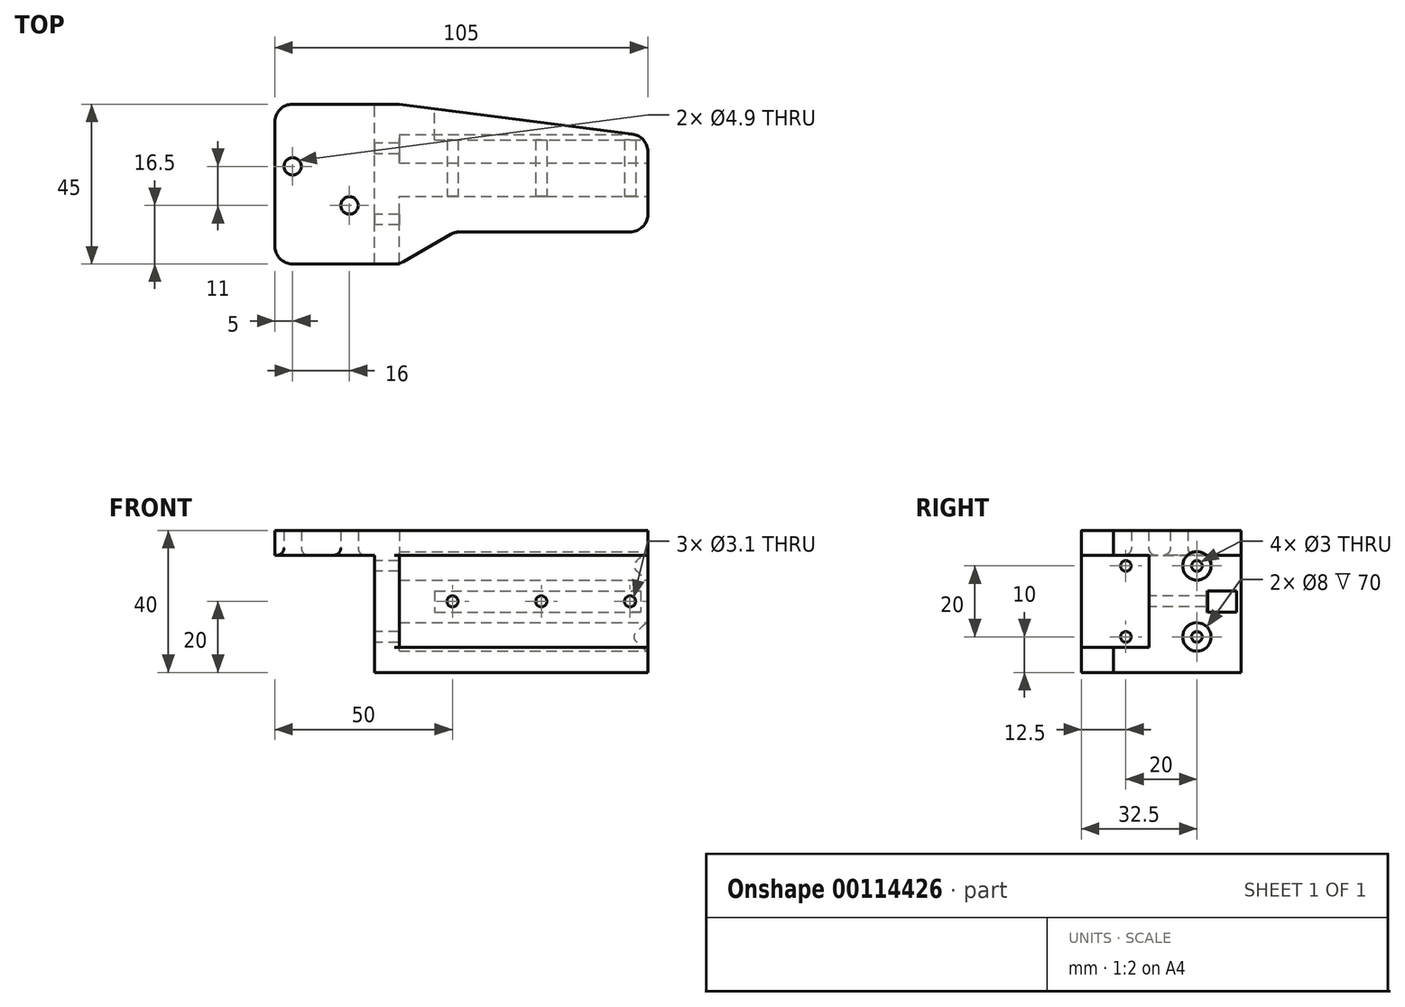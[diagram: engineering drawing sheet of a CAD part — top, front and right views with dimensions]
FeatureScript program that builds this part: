
annotation { "Feature Type Name" : "Feature", "Feature Type Description" : "" }
export const myFeature = defineFeature(function(context is Context, id is Id, definition is map)
    precondition{}
    {
        {
            var Q0;
            Q0=qCreatedBy(makeId("Top.planeOp"),FACE);
            var sketch = newSketch(context, id + "F0", { "sketchPlane" : qUnion([Q0])});
            skLineSegment(sketch, "E0.bottom", {"start": v(0, 0) * mm, "end": v(5.66, 0) * mm});
            skLineSegment(sketch, "E0.top", {"start": v(0, 45) * mm, "end": v(7, 45) * mm});
            skLineSegment(sketch, "E0.left", {"start": v(0, 0) * mm, "end": v(0, 45) * mm});
            skLineSegment(sketch, "E1", {"start": v(7, 45) * mm, "end": v(72.64, 36.56) * mm});
            skLineSegment(sketch, "E2", {"start": v(72, 9) * mm, "end": v(23.93, 9) * mm});
            skLineSegment(sketch, "E3", {"start": v(21.43, 8.33) * mm, "end": v(8.16, 0.67) * mm});
            skLineSegment(sketch, "E4", {"start": v(77, 31.6) * mm, "end": v(77, 14) * mm});
            skPoint(sketch, "E5.visualSharp", {"position": v(77, 36) * mm});
            skArc(sketch, "E5.filletArc", {"start": v(77, 31.6) * mm, "mid": v(75.75, 34.9) * mm, "end": v(72.64, 36.56) * mm});
            skPoint(sketch, "E6.visualSharp", {"position": v(77, 9) * mm});
            skArc(sketch, "E6.filletArc", {"start": v(72, 9) * mm, "mid": v(75.54, 10.46) * mm, "end": v(77, 14) * mm});
            skPoint(sketch, "E7.visualSharp", {"position": v(22.59, 9) * mm});
            skArc(sketch, "E7.filletArc", {"start": v(23.93, 9) * mm, "mid": v(22.63, 8.83) * mm, "end": v(21.43, 8.33) * mm});
            skPoint(sketch, "E8.visualSharp", {"position": v(7, 0) * mm});
            skArc(sketch, "E8.filletArc", {"start": v(5.66, 0) * mm, "mid": v(6.95, 0.17) * mm, "end": v(8.16, 0.67) * mm});
            skSolve(sketch);
        }
        {
            var Q0;
            Q0 = qSketchRegion(id + "F0", true);
            extrude(context, id + "F1", {"entities" : qUnion([Q0]), "depth" : 7 * mm});
        }
        {
            var Q0;
            Q0=makeQuery(id+"F1.opExtrude","CAP_FACE",FACE,{"disambiguationData":[OSD([sQuery(id+"F0.wireOp",EDGE,"E0.bottom"),sQuery(id+"F0.wireOp",EDGE,"E0.top"),sQuery(id+"F0.wireOp",EDGE,"E0.left"),sQuery(id+"F0.wireOp",EDGE,"E1"),sQuery(id+"F0.wireOp",EDGE,"E2"),sQuery(id+"F0.wireOp",EDGE,"E3"),sQuery(id+"F0.wireOp",EDGE,"E4")])],"isStart":false});
            var sketch = newSketch(context, id + "F2", { "sketchPlane" : qUnion([Q0])});
            skLineSegment(sketch, "E9.bottom", {"start": v(0, 0) * mm, "end": v(7, 0) * mm});
            skLineSegment(sketch, "E9.top", {"start": v(0, 45) * mm, "end": v(7, 45) * mm});
            skLineSegment(sketch, "E9.left", {"start": v(0, 0) * mm, "end": v(0, 45) * mm});
            skLineSegment(sketch, "E9.right", {"start": v(7, 0) * mm, "end": v(7, 19) * mm});
            skLineSegment(sketch, "E10", {"start": v(7, 19) * mm, "end": v(77, 19) * mm});
            skLineSegment(sketch, "E11", {"start": v(7, 45) * mm, "end": v(7, 45) * mm});
            skLineSegment(sketch, "E12", {"start": v(77, 19) * mm, "end": v(77, 31.6) * mm});
            skLineSegment(sketch, "E13", {"start": v(72.64, 36.56) * mm, "end": v(7, 45) * mm});
            skPoint(sketch, "E14.visualSharp", {"position": v(77, 36) * mm});
            skArc(sketch, "E14.filletArc", {"start": v(77, 31.6) * mm, "mid": v(75.75, 34.9) * mm, "end": v(72.64, 36.56) * mm});
            skSolve(sketch);
        }
        {
            var Q0;
            Q0 = qSketchRegion(id + "F2", true);
            extrude(context, id + "F3", {"entities" : qUnion([Q0]), "operationType" : NewBodyOperationType.ADD, "depth" : (40 - 7 * 2) * mm});
        }
        {
            var Q0;
            Q0=makeQuery(id+"F3.opExtrude","CAP_FACE",FACE,{"disambiguationData":[OSD([sQuery(id+"F2.wireOp",EDGE,"E9.bottom"),sQuery(id+"F2.wireOp",EDGE,"E9.top"),sQuery(id+"F2.wireOp",EDGE,"E9.left"),sQuery(id+"F2.wireOp",EDGE,"E9.right"),sQuery(id+"F2.wireOp",EDGE,"E10"),sQuery(id+"F2.wireOp",EDGE,"o3z8yJx9-oVSc-GKtG-S4sG-GDwT2Ib3WAK0"),sQuery(id+"F2.wireOp",EDGE,"E11")])],"isStart":false});
            var sketch = newSketch(context, id + "F4", { "sketchPlane" : qUnion([Q0])});
            skLineSegment(sketch, "E15", {"start": v(0, 0) * mm, "end": v(5.66, 0) * mm});
            skLineSegment(sketch, "E16", {"start": v(8.16, 0.67) * mm, "end": v(21.48, 8.36) * mm});
            skLineSegment(sketch, "E17", {"start": v(23.98, 9.03) * mm, "end": v(72, 9.03) * mm});
            skLineSegment(sketch, "E18", {"start": v(0, 45) * mm, "end": v(0, 45) * mm});
            skLineSegment(sketch, "E19", {"start": v(0, 45) * mm, "end": v(0, 0) * mm, "construction": true});
            skLineSegment(sketch, "E20.bottom", {"start": v(0, 45) * mm, "end": v(-23, 45) * mm});
            skLineSegment(sketch, "E20.top", {"start": v(0, 0) * mm, "end": v(-23, 0) * mm});
            skLineSegment(sketch, "E20.left", {"start": v(0, 45) * mm, "end": v(0, 0) * mm});
            skLineSegment(sketch, "E20.right", {"start": v(-28, 40) * mm, "end": v(-28, 5) * mm});
            skCircle(sketch, "E21", {"center": v(-23, 27.5) * mm, "radius": 2.45 * mm});
            skCircle(sketch, "E22", {"center": v(-7, 16.5) * mm, "radius": 2.45 * mm});
            skLineSegment(sketch, "E23", {"start": v(-38.46, 22) * mm, "end": v(86.28, 22) * mm, "construction": true});
            skPoint(sketch, "E24.visualSharp", {"position": v(-28, 45) * mm});
            skArc(sketch, "E24.filletArc", {"start": v(-23, 45) * mm, "mid": v(-26.54, 43.54) * mm, "end": v(-28, 40) * mm});
            skPoint(sketch, "E25.visualSharp", {"position": v(-28, 0) * mm});
            skArc(sketch, "E25.filletArc", {"start": v(-28, 5) * mm, "mid": v(-26.54, 1.46) * mm, "end": v(-23, 0) * mm});
            skPoint(sketch, "E26.visualSharp", {"position": v(7, 0) * mm});
            skArc(sketch, "E26.filletArc", {"start": v(5.66, 0) * mm, "mid": v(6.95, 0.17) * mm, "end": v(8.16, 0.67) * mm});
            skPoint(sketch, "E27.visualSharp", {"position": v(22.64, 9.03) * mm});
            skArc(sketch, "E27.filletArc", {"start": v(23.98, 9.03) * mm, "mid": v(22.69, 8.86) * mm, "end": v(21.48, 8.36) * mm});
            skPoint(sketch, "E28.visualSharp", {"position": v(77, 9.03) * mm});
            skLineSegment(sketch, "E29", {"start": v(0, 45) * mm, "end": v(7, 45) * mm});
            skLineSegment(sketch, "E30", {"start": v(7, 45) * mm, "end": v(72.64, 36.6) * mm});
            skLineSegment(sketch, "E31", {"start": v(77, 31.63) * mm, "end": v(77, 14.03) * mm});
            skPoint(sketch, "E32.visualSharp", {"position": v(77, 36.03) * mm});
            skArc(sketch, "E32.filletArc", {"start": v(77, 31.63) * mm, "mid": v(75.75, 34.93) * mm, "end": v(72.64, 36.6) * mm});
            skArc(sketch, "E33.filletArc", {"start": v(72, 9.03) * mm, "mid": v(75.54, 10.5) * mm, "end": v(77, 14.03) * mm});
            skSolve(sketch);
        }
        {
            var Q0;
            Q0 = qSketchRegion(id + "F4", true);
            extrude(context, id + "F5", {"entities" : qUnion([Q0]), "operationType" : NewBodyOperationType.ADD, "depth" : 7 * mm});
        }
        {
            var Q0;
            Q0=makeQuery(id+"F5.opExtrude","CAP_EDGE",EDGE,{"disambiguationData":[OSD([sQuery(id+"F4.wireOp",EDGE,"E22")])],"isStart":true});
            var Q1;
            Q1=makeQuery(id+"F5.opExtrude","CAP_EDGE",EDGE,{"disambiguationData":[OSD([sQuery(id+"F4.wireOp",EDGE,"E21")])],"isStart":true});
            fillet(context, id + "F6", {"entities" : qUnion([Q0, Q1]), "radius" : 2 * mm, "tangentPropagation" : true, "allowEdgeOverflow" : false});
        }
        {
            var Q0;
            Q0=makeQuery(id+"F3.boolean.opBoolean","MERGE",FACE,{"derivedFrom":[makeQuery(id+"F1.opExtrude","SWEPT_FACE",FACE,{"disambiguationData":[OSD([sQuery(id+"F0.wireOp",EDGE,"E0.left")])]}),makeQuery(id+"F3.opExtrude","SWEPT_FACE",FACE,{"disambiguationData":[OSD([sQuery(id+"F2.wireOp",EDGE,"E9.left")])]})]});
            var sketch = newSketch(context, id + "F7", { "sketchPlane" : qUnion([Q0])});
            skCircle(sketch, "E34", {"center": v(-32.5, 30) * mm, "radius": 1.5 * mm});
            skCircle(sketch, "E35", {"center": v(-12.5, 30) * mm, "radius": 1.5 * mm});
            skCircle(sketch, "E36", {"center": v(-12.5, 10) * mm, "radius": 1.5 * mm});
            skCircle(sketch, "E37", {"center": v(-32.5, 10) * mm, "radius": 1.5 * mm});
            skSolve(sketch);
        }
        {
            var Q0;
            Q0 = qSketchRegion(id + "F7", true);
            extrude(context, id + "F8", {"entities" : qUnion([Q0]), "operationType" : NewBodyOperationType.REMOVE, "endBound" : BoundingType.THROUGH_ALL, "oppositeDirection" : true, "depth" : 25 * mm});
        }
        {
            var Q0;
            Q0=makeQuery(id+"F5.boolean.opBoolean","MERGE",FACE,{"derivedFrom":[makeQuery(id+"F3.boolean.opBoolean","MERGE",FACE,{"derivedFrom":[makeQuery(id+"F1.opExtrude","SWEPT_FACE",FACE,{"disambiguationData":[OSD([sQuery(id+"F0.wireOp",EDGE,"E4")])]}),makeQuery(id+"F3.opExtrude","SWEPT_FACE",FACE,{"disambiguationData":[OSD([sQuery(id+"F2.wireOp",EDGE,"E12")])]})]}),makeQuery(id+"F5.opExtrude","SWEPT_FACE",FACE,{"disambiguationData":[OSD([sQuery(id+"F4.wireOp",EDGE,"E31")])]})]});
            var sketch = newSketch(context, id + "F9", { "sketchPlane" : qUnion([Q0])});
            skCircle(sketch, "E38", {"center": v(32.5, 30) * mm, "radius": 4 * mm});
            skCircle(sketch, "E39", {"center": v(32.5, 10) * mm, "radius": 4 * mm});
            skSolve(sketch);
        }
        {
            var Q0;
            Q0 = qSketchRegion(id + "F9", true);
            extrude(context, id + "F10", {"entities" : qUnion([Q0]), "operationType" : NewBodyOperationType.REMOVE, "oppositeDirection" : true, "depth" : 70 * mm});
        }
        {
            var Q0;
            Q0=makeQuery(id+"F3.opExtrude","SWEPT_FACE",FACE,{"disambiguationData":[OSD([sQuery(id+"F2.wireOp",EDGE,"E10")])]});
            var sketch = newSketch(context, id + "F11", { "sketchPlane" : qUnion([Q0])});
            skCircle(sketch, "E40", {"center": v(22, 20) * mm, "radius": 1.55 * mm});
            skCircle(sketch, "E41", {"center": v(47, 20) * mm, "radius": 1.55 * mm});
            skCircle(sketch, "E42", {"center": v(72, 20) * mm, "radius": 1.55 * mm});
            skSolve(sketch);
        }
        {
            var Q0;
            Q0 = qSketchRegion(id + "F11", true);
            extrude(context, id + "F12", {"entities" : qUnion([Q0]), "operationType" : NewBodyOperationType.REMOVE, "endBound" : BoundingType.THROUGH_ALL, "oppositeDirection" : true, "depth" : 25 * mm});
        }
        {
            var Q0;
            Q0=makeQuery(id+"F5.boolean.opBoolean","MERGE",FACE,{"derivedFrom":[makeQuery(id+"F3.boolean.opBoolean","MERGE",FACE,{"derivedFrom":[makeQuery(id+"F1.opExtrude","SWEPT_FACE",FACE,{"disambiguationData":[OSD([sQuery(id+"F0.wireOp",EDGE,"E0.top")])]}),makeQuery(id+"F3.opExtrude","SWEPT_FACE",FACE,{"disambiguationData":[OSD([sQuery(id+"F2.wireOp",EDGE,"E9.top")])]})]}),makeQuery(id+"F5.opExtrude","SWEPT_FACE",FACE,{"disambiguationData":[OSD([sQuery(id+"F4.wireOp",EDGE,"E20.bottom"),sQuery(id+"F4.wireOp",EDGE,"E29")])]})]});
            var sketch = newSketch(context, id + "F13", { "sketchPlane" : qUnion([Q0])});
            skLineSegment(sketch, "E43.bottom", {"start": v(-17, 23) * mm, "end": v(-75, 23) * mm});
            skLineSegment(sketch, "E43.top", {"start": v(-17, 17) * mm, "end": v(-75, 17) * mm});
            skLineSegment(sketch, "E43.left", {"start": v(-17, 23) * mm, "end": v(-17, 17) * mm});
            skLineSegment(sketch, "E43.right", {"start": v(-75, 23) * mm, "end": v(-75, 17) * mm});
            skSolve(sketch);
        }
        {
            var Q0;
            Q0 = qSketchRegion(id + "F13", true);
            extrude(context, id + "F14", {"entities" : qUnion([Q0]), "operationType" : NewBodyOperationType.REMOVE, "oppositeDirection" : true, "depth" : 10 * mm});
        }
    });
